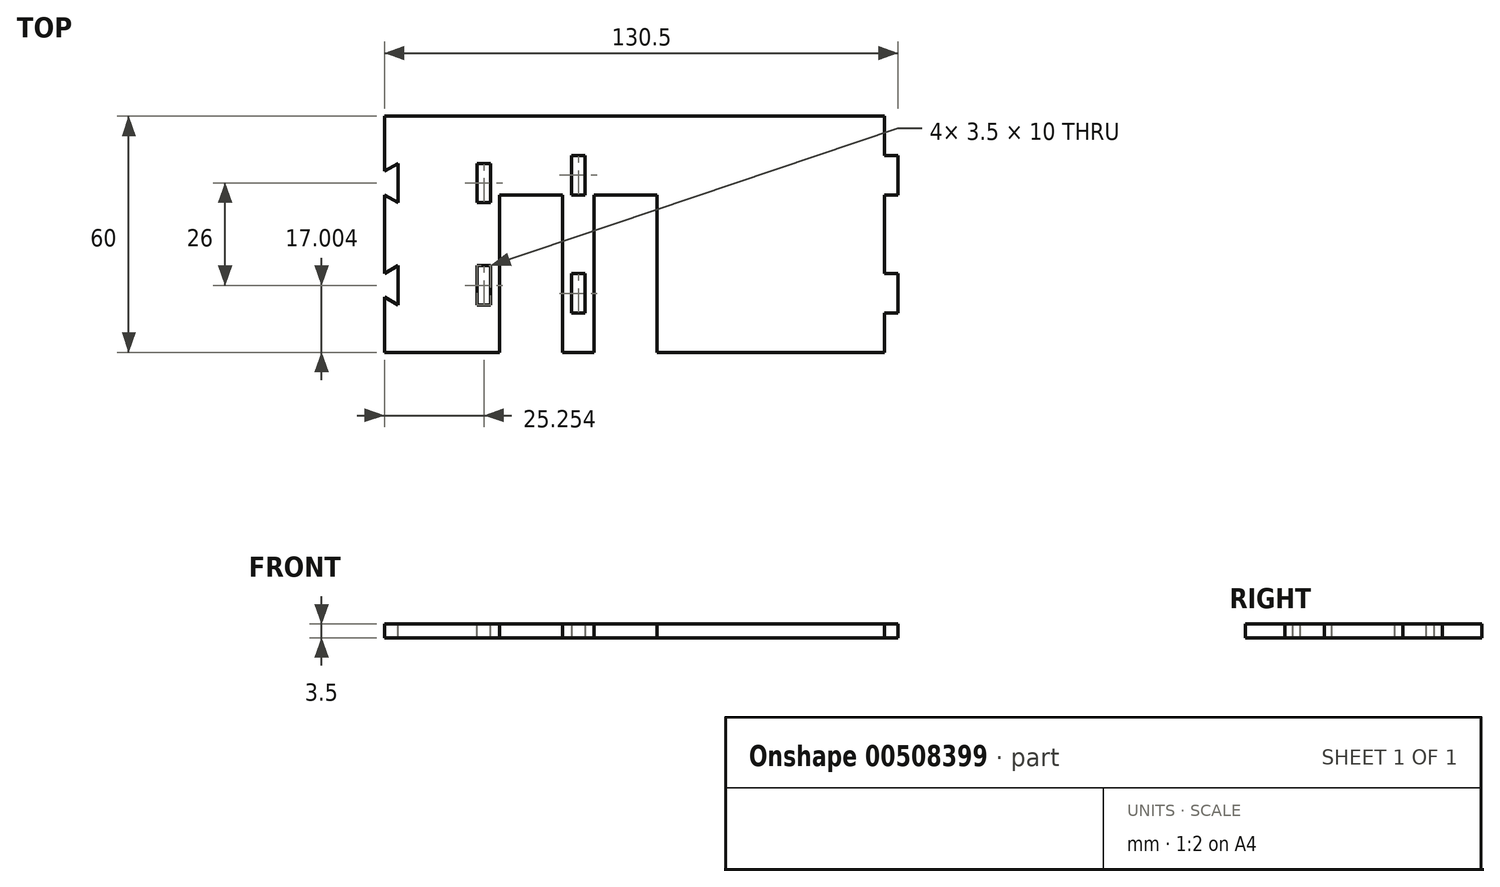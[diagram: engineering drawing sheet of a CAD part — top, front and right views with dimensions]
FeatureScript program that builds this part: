
annotation { "Feature Type Name" : "Feature", "Feature Type Description" : "" }
export const myFeature = defineFeature(function(context is Context, id is Id, definition is map)
    precondition{}
    {
        {
            var Q0;
            Q0=qCreatedBy(makeId("Top.planeOp"),FACE);
            var sketch = newSketch(context, id + "F0", { "sketchPlane" : qUnion([Q0])});
            skLineSegment(sketch, "E0", {"start": v(-49.3, -25.56) * mm, "end": v(-23.56, -25.56) * mm});
            skLineSegment(sketch, "E1", {"start": v(-23.56, -25.56) * mm, "end": v(-23.56, 14.44) * mm});
            skLineSegment(sketch, "E2", {"start": v(-23.56, 14.44) * mm, "end": v(-7.56, 14.44) * mm});
            skLineSegment(sketch, "E3", {"start": v(-7.56, 14.44) * mm, "end": v(-7.56, -25.56) * mm});
            skLineSegment(sketch, "E4", {"start": v(-7.56, -25.56) * mm, "end": v(-5.3, -25.56) * mm});
            skLineSegment(sketch, "E5", {"start": v(-5.3, 34.44) * mm, "end": v(-49.3, 34.44) * mm});
            skLineSegment(sketch, "E6", {"start": v(-49.3, 34.44) * mm, "end": v(-49.3, -25.56) * mm});
            skLineSegment(sketch, "E7", {"start": v(-1.8, -25.56) * mm, "end": v(0.44, -25.56) * mm});
            skLineSegment(sketch, "E8", {"start": v(0.44, -25.56) * mm, "end": v(0.44, 14.44) * mm});
            skLineSegment(sketch, "E9", {"start": v(0.44, 14.44) * mm, "end": v(16.44, 14.44) * mm});
            skLineSegment(sketch, "E10", {"start": v(16.44, 14.44) * mm, "end": v(16.44, -25.56) * mm});
            skLineSegment(sketch, "E11", {"start": v(16.44, -25.56) * mm, "end": v(74.2, -25.56) * mm});
            skLineSegment(sketch, "E12", {"start": v(74.2, -25.56) * mm, "end": v(74.2, 34.44) * mm});
            skLineSegment(sketch, "E13", {"start": v(74.2, 34.44) * mm, "end": v(-1.8, 34.44) * mm});
            skLineSegment(sketch, "E14", {"start": v(-1.8, 34.44) * mm, "end": v(-5.3, 34.44) * mm});
            skLineSegment(sketch, "E15", {"start": v(-5.3, -25.56) * mm, "end": v(-1.8, -25.56) * mm});
            skLineSegment(sketch, "E16", {"start": v(-1.8, 24.44) * mm, "end": v(-1.8, 14.44) * mm});
            skLineSegment(sketch, "E17", {"start": v(-1.8, -5.56) * mm, "end": v(-1.8, -15.56) * mm});
            skLineSegment(sketch, "E18", {"start": v(-1.8, -15.56) * mm, "end": v(-5.3, -15.56) * mm});
            skLineSegment(sketch, "E19", {"start": v(-5.3, -15.56) * mm, "end": v(-5.3, -5.56) * mm});
            skLineSegment(sketch, "E20", {"start": v(-5.3, -5.56) * mm, "end": v(-1.8, -5.56) * mm});
            skLineSegment(sketch, "E21", {"start": v(-1.8, 24.44) * mm, "end": v(-5.3, 24.44) * mm});
            skLineSegment(sketch, "E22", {"start": v(-5.3, 24.44) * mm, "end": v(-5.3, 14.44) * mm});
            skLineSegment(sketch, "E23", {"start": v(-5.3, 14.44) * mm, "end": v(-1.8, 14.44) * mm});
            skSolve(sketch);
        }
        {
            var Q0;
            Q0=makeQuery(id+"F0.imprint","IMPRINT",FACE,{"disambiguationData":[TD([[makeQuery(id+"F0.imprint","IMPRINT",EDGE,{"derivedFrom":sQuery(id+"F0.wireOp",EDGE,"E0")}),1.0]])]});
            extrude(context, id + "F1", {"entities" : qUnion([Q0]), "depth" : 3.5 * mm, "offsetDistance" : 25 * mm});
        }
        {
            var Q0;
            Q0=makeQuery(id+"F1.opExtrude","SWEPT_FACE",FACE,{"disambiguationData":[OSD([sQuery(id+"F0.wireOp",EDGE,"E6")])]});
            extrude(context, id + "F2", {"entities" : qUnion([Q0]), "operationType" : NewBodyOperationType.ADD, "depth" : 3.5 * mm, "offsetDistance" : 25 * mm});
        }
        {
            var Q0;
            {var subQ0=sQuery(id+"F0.wireOp",EDGE,"E6");Q0=makeQuery(id+"F2.boolean.opBoolean","MERGE",FACE,{"derivedFrom":[makeQuery(id+"F1.opExtrude","CAP_FACE",FACE,{"disambiguationData":[OSD([sQuery(id+"F0.wireOp",EDGE,"E0"),sQuery(id+"F0.wireOp",EDGE,"E1"),sQuery(id+"F0.wireOp",EDGE,"E2"),sQuery(id+"F0.wireOp",EDGE,"E3"),sQuery(id+"F0.wireOp",EDGE,"E4"),sQuery(id+"F0.wireOp",EDGE,"E5"),subQ0,sQuery(id+"F0.wireOp",EDGE,"E7"),sQuery(id+"F0.wireOp",EDGE,"E8"),sQuery(id+"F0.wireOp",EDGE,"E9"),sQuery(id+"F0.wireOp",EDGE,"E10"),sQuery(id+"F0.wireOp",EDGE,"E11"),sQuery(id+"F0.wireOp",EDGE,"E12"),sQuery(id+"F0.wireOp",EDGE,"E13"),sQuery(id+"F0.wireOp",EDGE,"E14"),sQuery(id+"F0.wireOp",EDGE,"E15"),sQuery(id+"F0.wireOp",EDGE,"E16"),sQuery(id+"F0.wireOp",EDGE,"E17"),sQuery(id+"F0.wireOp",EDGE,"E18"),sQuery(id+"F0.wireOp",EDGE,"E19"),sQuery(id+"F0.wireOp",EDGE,"E20"),sQuery(id+"F0.wireOp",EDGE,"E21"),sQuery(id+"F0.wireOp",EDGE,"E22"),sQuery(id+"F0.wireOp",EDGE,"E23")])],"isStart":false}),makeQuery(id+"F2.opExtrude","SWEPT_FACE",FACE,{"disambiguationData":[OSD([subQ0]),TDD([makeQuery(id+"F1.opExtrude","CAP_EDGE",EDGE,{"disambiguationData":[OSD([subQ0])],"isStart":false})])]})]});}
            var sketch = newSketch(context, id + "F3", { "sketchPlane" : qUnion([Q0])});
            skLineSegment(sketch, "E24", {"start": v(-52.8, 34.44) * mm, "end": v(-52.8, 20.44) * mm});
            skLineSegment(sketch, "E25", {"start": v(-52.8, 14.44) * mm, "end": v(-52.8, -5.56) * mm});
            skLineSegment(sketch, "E26", {"start": v(-52.8, -11.56) * mm, "end": v(-52.8, -25.56) * mm});
            skLineSegment(sketch, "E27", {"start": v(-52.8, -25.56) * mm, "end": v(-49.3, -25.56) * mm});
            skLineSegment(sketch, "E28", {"start": v(-49.3, -13.56) * mm, "end": v(-49.3, -3.56) * mm});
            skLineSegment(sketch, "E29", {"start": v(-49.3, 12.44) * mm, "end": v(-49.3, 22.44) * mm});
            skLineSegment(sketch, "E30", {"start": v(-49.3, 34.44) * mm, "end": v(-52.8, 34.44) * mm});
            skLineSegment(sketch, "E31", {"start": v(-49.3, 22.44) * mm, "end": v(-52.8, 20.44) * mm});
            skLineSegment(sketch, "E32", {"start": v(-52.8, 14.44) * mm, "end": v(-49.3, 12.44) * mm});
            skLineSegment(sketch, "E33", {"start": v(-49.3, -13.56) * mm, "end": v(-52.8, -11.56) * mm});
            skLineSegment(sketch, "E34", {"start": v(-52.8, -5.56) * mm, "end": v(-49.3, -3.56) * mm});
            skSolve(sketch);
        }
        {
            var Q0;
            Q0=makeQuery(id+"F3.imprint","IMPRINT",FACE,{"disambiguationData":[TD([[makeQuery(id+"F3.imprint","IMPRINT",EDGE,{"derivedFrom":sQuery(id+"F3.wireOp",EDGE,"E29")}),1.0]])]});
            var Q1;
            Q1=makeQuery(id+"F3.imprint","IMPRINT",FACE,{"disambiguationData":[TD([[makeQuery(id+"F3.imprint","IMPRINT",EDGE,{"derivedFrom":sQuery(id+"F3.wireOp",EDGE,"E28")}),1.0]])]});
            extrude(context, id + "F4", {"entities" : qUnion([Q0, Q1]), "operationType" : NewBodyOperationType.REMOVE, "oppositeDirection" : true, "depth" : 3.5 * mm, "offsetDistance" : 25 * mm});
        }
        {
            var Q0;
            Q0=makeQuery(id+"F1.opExtrude","SWEPT_FACE",FACE,{"disambiguationData":[OSD([sQuery(id+"F0.wireOp",EDGE,"E12")])]});
            var sketch = newSketch(context, id + "F5", { "sketchPlane" : qUnion([Q0])});
            skLineSegment(sketch, "E35", {"start": v(34.44, 0) * mm, "end": v(24.44, 0) * mm});
            skLineSegment(sketch, "E36", {"start": v(24.44, 0) * mm, "end": v(14.44, 0) * mm});
            skLineSegment(sketch, "E37", {"start": v(14.44, 0) * mm, "end": v(-5.56, 0) * mm});
            skLineSegment(sketch, "E38", {"start": v(-5.56, 0) * mm, "end": v(-15.56, 0) * mm});
            skLineSegment(sketch, "E39", {"start": v(-15.56, 0) * mm, "end": v(-25.56, 0) * mm});
            skLineSegment(sketch, "E40", {"start": v(24.44, 0) * mm, "end": v(24.44, 3.5) * mm});
            skLineSegment(sketch, "E41", {"start": v(24.44, 3.5) * mm, "end": v(14.44, 3.5) * mm});
            skLineSegment(sketch, "E42", {"start": v(14.44, 3.5) * mm, "end": v(14.44, 0) * mm});
            skLineSegment(sketch, "E43", {"start": v(-5.56, 0) * mm, "end": v(-5.56, 3.5) * mm});
            skLineSegment(sketch, "E44", {"start": v(-15.56, 0) * mm, "end": v(-15.56, 3.5) * mm});
            skLineSegment(sketch, "E45", {"start": v(-15.56, 3.5) * mm, "end": v(-5.56, 3.5) * mm});
            skSolve(sketch);
        }
        {
            var Q0;
            Q0=makeQuery(id+"F5.imprint","IMPRINT",FACE,{"disambiguationData":[TD([[makeQuery(id+"F5.imprint","IMPRINT",EDGE,{"derivedFrom":sQuery(id+"F5.wireOp",EDGE,"E38")}),1.0]])]});
            var Q1;
            Q1=makeQuery(id+"F5.imprint","IMPRINT",FACE,{"disambiguationData":[TD([[makeQuery(id+"F5.imprint","IMPRINT",EDGE,{"derivedFrom":sQuery(id+"F5.wireOp",EDGE,"E36")}),1.0]])]});
            extrude(context, id + "F6", {"entities" : qUnion([Q0, Q1]), "operationType" : NewBodyOperationType.ADD, "depth" : 3.5 * mm, "offsetDistance" : 25 * mm});
        }
        {
            var Q0;
            {var subQ0=sQuery(id+"F0.wireOp",EDGE,"E6");Q0=makeQuery(id+"F6.boolean.opBoolean","MERGE",FACE,{"derivedFrom":[makeQuery(id+"F2.boolean.opBoolean","MERGE",FACE,{"derivedFrom":[makeQuery(id+"F1.opExtrude","CAP_FACE",FACE,{"disambiguationData":[OSD([sQuery(id+"F0.wireOp",EDGE,"E0"),sQuery(id+"F0.wireOp",EDGE,"E1"),sQuery(id+"F0.wireOp",EDGE,"E2"),sQuery(id+"F0.wireOp",EDGE,"E3"),sQuery(id+"F0.wireOp",EDGE,"E4"),sQuery(id+"F0.wireOp",EDGE,"E5"),subQ0,sQuery(id+"F0.wireOp",EDGE,"E7"),sQuery(id+"F0.wireOp",EDGE,"E8"),sQuery(id+"F0.wireOp",EDGE,"E9"),sQuery(id+"F0.wireOp",EDGE,"E10"),sQuery(id+"F0.wireOp",EDGE,"E11"),sQuery(id+"F0.wireOp",EDGE,"E12"),sQuery(id+"F0.wireOp",EDGE,"E13"),sQuery(id+"F0.wireOp",EDGE,"E14"),sQuery(id+"F0.wireOp",EDGE,"E15"),sQuery(id+"F0.wireOp",EDGE,"E16"),sQuery(id+"F0.wireOp",EDGE,"E17"),sQuery(id+"F0.wireOp",EDGE,"E18"),sQuery(id+"F0.wireOp",EDGE,"E19"),sQuery(id+"F0.wireOp",EDGE,"E20"),sQuery(id+"F0.wireOp",EDGE,"E21"),sQuery(id+"F0.wireOp",EDGE,"E22"),sQuery(id+"F0.wireOp",EDGE,"E23")])],"isStart":false}),makeQuery(id+"F2.opExtrude","SWEPT_FACE",FACE,{"disambiguationData":[OSD([subQ0]),TDD([makeQuery(id+"F1.opExtrude","CAP_EDGE",EDGE,{"disambiguationData":[OSD([subQ0])],"isStart":false})])]})]}),makeQuery(id+"F6.opExtrude","SWEPT_FACE",FACE,{"disambiguationData":[OSD([sQuery(id+"F5.wireOp",EDGE,"E41")])]}),makeQuery(id+"F6.opExtrude","SWEPT_FACE",FACE,{"disambiguationData":[OSD([sQuery(id+"F5.wireOp",EDGE,"E45")])]})]});}
            var sketch = newSketch(context, id + "F7", { "sketchPlane" : qUnion([Q0])});
            skLineSegment(sketch, "E46", {"start": v(-23.56, -25.56) * mm, "end": v(-25.8, -25.56) * mm});
            skLineSegment(sketch, "E47", {"start": v(-25.8, -25.56) * mm, "end": v(-29.3, -25.56) * mm});
            skLineSegment(sketch, "E48", {"start": v(-25.8, -13.56) * mm, "end": v(-25.8, -3.56) * mm});
            skLineSegment(sketch, "E49", {"start": v(-25.8, 12.44) * mm, "end": v(-25.8, 22.44) * mm});
            skLineSegment(sketch, "E50", {"start": v(-25.8, 22.44) * mm, "end": v(-29.3, 22.44) * mm});
            skLineSegment(sketch, "E51", {"start": v(-29.3, 22.44) * mm, "end": v(-29.3, 12.44) * mm});
            skLineSegment(sketch, "E52", {"start": v(-29.3, 12.44) * mm, "end": v(-25.8, 12.44) * mm});
            skLineSegment(sketch, "E53", {"start": v(-25.8, -3.56) * mm, "end": v(-29.3, -3.56) * mm});
            skLineSegment(sketch, "E54", {"start": v(-29.3, -3.56) * mm, "end": v(-29.3, -13.56) * mm});
            skLineSegment(sketch, "E55", {"start": v(-29.3, -13.56) * mm, "end": v(-25.8, -13.56) * mm});
            skSolve(sketch);
        }
        {
            var Q0;
            Q0=makeQuery(id+"F7.imprint","IMPRINT",FACE,{"disambiguationData":[TD([[makeQuery(id+"F7.imprint","IMPRINT",EDGE,{"derivedFrom":sQuery(id+"F7.wireOp",EDGE,"E49")}),1.0]])]});
            var Q1;
            Q1=makeQuery(id+"F7.imprint","IMPRINT",FACE,{"disambiguationData":[TD([[makeQuery(id+"F7.imprint","IMPRINT",EDGE,{"derivedFrom":sQuery(id+"F7.wireOp",EDGE,"E48")}),1.0]])]});
            extrude(context, id + "F8", {"entities" : qUnion([Q0, Q1]), "operationType" : NewBodyOperationType.REMOVE, "oppositeDirection" : true, "depth" : 3.5 * mm, "offsetDistance" : 25 * mm});
        }
    });
